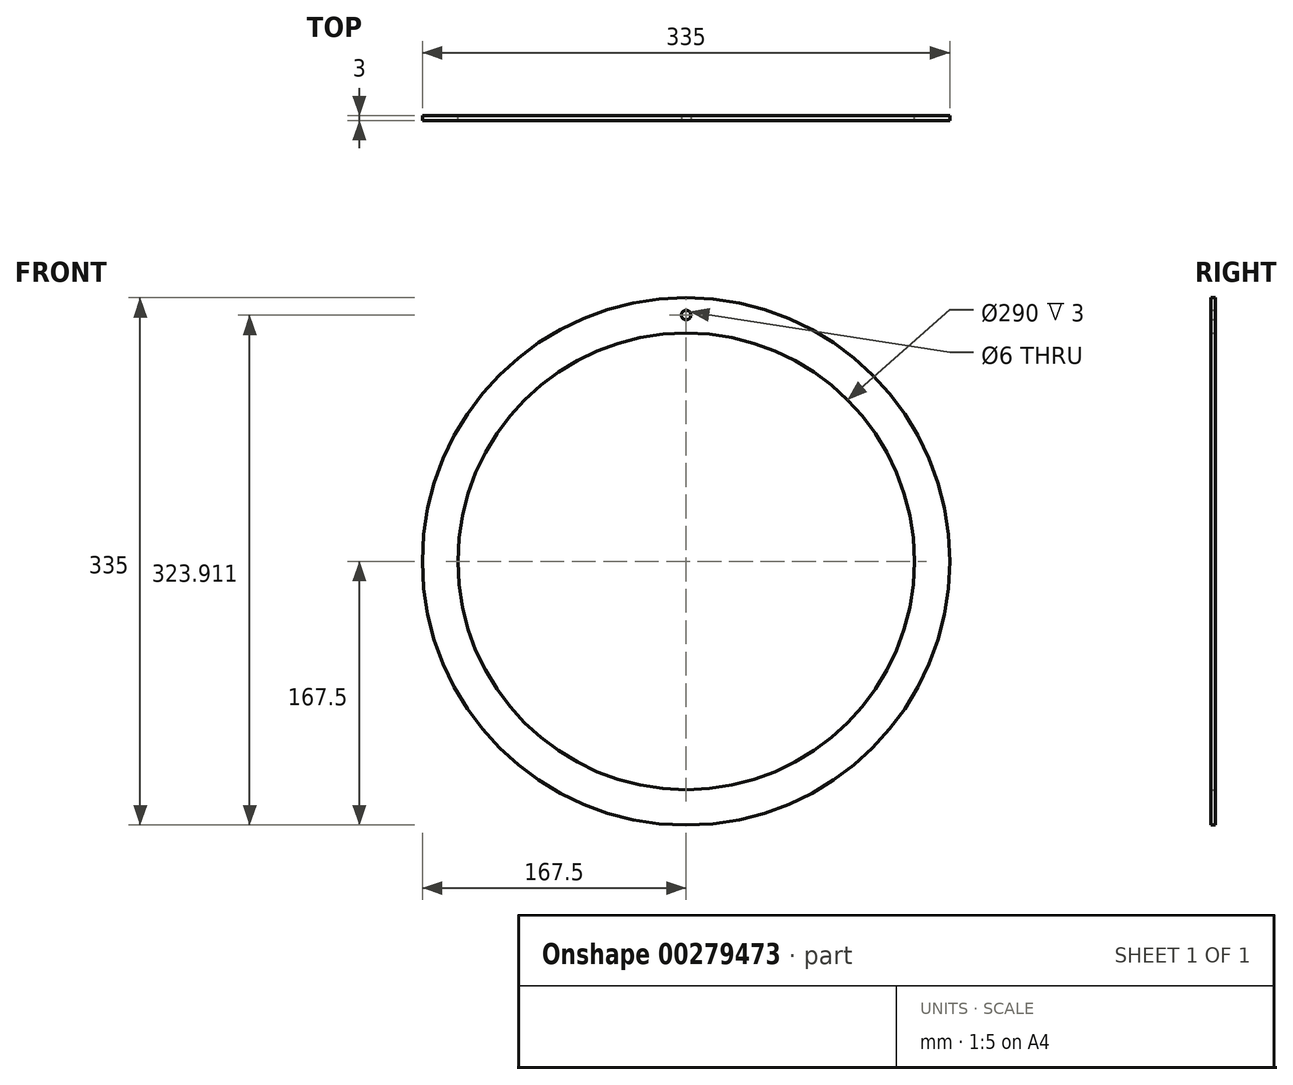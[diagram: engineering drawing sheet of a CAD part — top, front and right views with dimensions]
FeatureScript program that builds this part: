
annotation { "Feature Type Name" : "Feature", "Feature Type Description" : "" }
export const myFeature = defineFeature(function(context is Context, id is Id, definition is map)
    precondition{}
    {
        {
            var Q0;
            Q0=qCreatedBy(makeId("Front.planeOp"),FACE);
            var sketch = newSketch(context, id + "F0", { "sketchPlane" : qUnion([Q0])});
            skCircle(sketch, "E0", {"center": v(0, 0) * mm, "radius": 167.5 * mm});
            skCircle(sketch, "E1", {"center": v(0, 0) * mm, "radius": 145 * mm});
            skSolve(sketch);
        }
        {
            var Q0;
            Q0=qSketchRegion(id+"F0",true);
            extrude(context, id + "F1", {"entities" : qUnion([Q0]), "depth" : 3 * mm});
        }
        {
            var Q0;
            Q0=makeQuery(id+"F1.opExtrude","CAP_FACE",FACE,{"disambiguationData":[OSD([sQuery(id+"F0.wireOp",EDGE,"E0"),sQuery(id+"F0.wireOp",EDGE,"E1")])],"isStart":false});
            var sketch = newSketch(context, id + "F2", { "sketchPlane" : qUnion([Q0])});
            skCircle(sketch, "E2", {"center": v(0, 156.41) * mm, "radius": 3 * mm});
            skSolve(sketch);
        }
        {
            var Q0;
            Q0=makeQuery(id+"F2.imprint","IMPRINT",FACE,{"disambiguationData":[TD([[makeQuery(id+"F2.imprint","IMPRINT",EDGE,{"derivedFrom":sQuery(id+"F2.wireOp",EDGE,"E2")}),1.0]])]});
            var Q1;
            Q1=sQuery(id+"F2.wireOp",EDGE,"E2");
            extrude(context, id + "F3", {"entities" : qUnion([Q0]), "operationType" : NewBodyOperationType.REMOVE, "surfaceEntities" : qUnion([Q1]), "oppositeDirection" : true, "depth" : 25 * mm});
        }
    });
